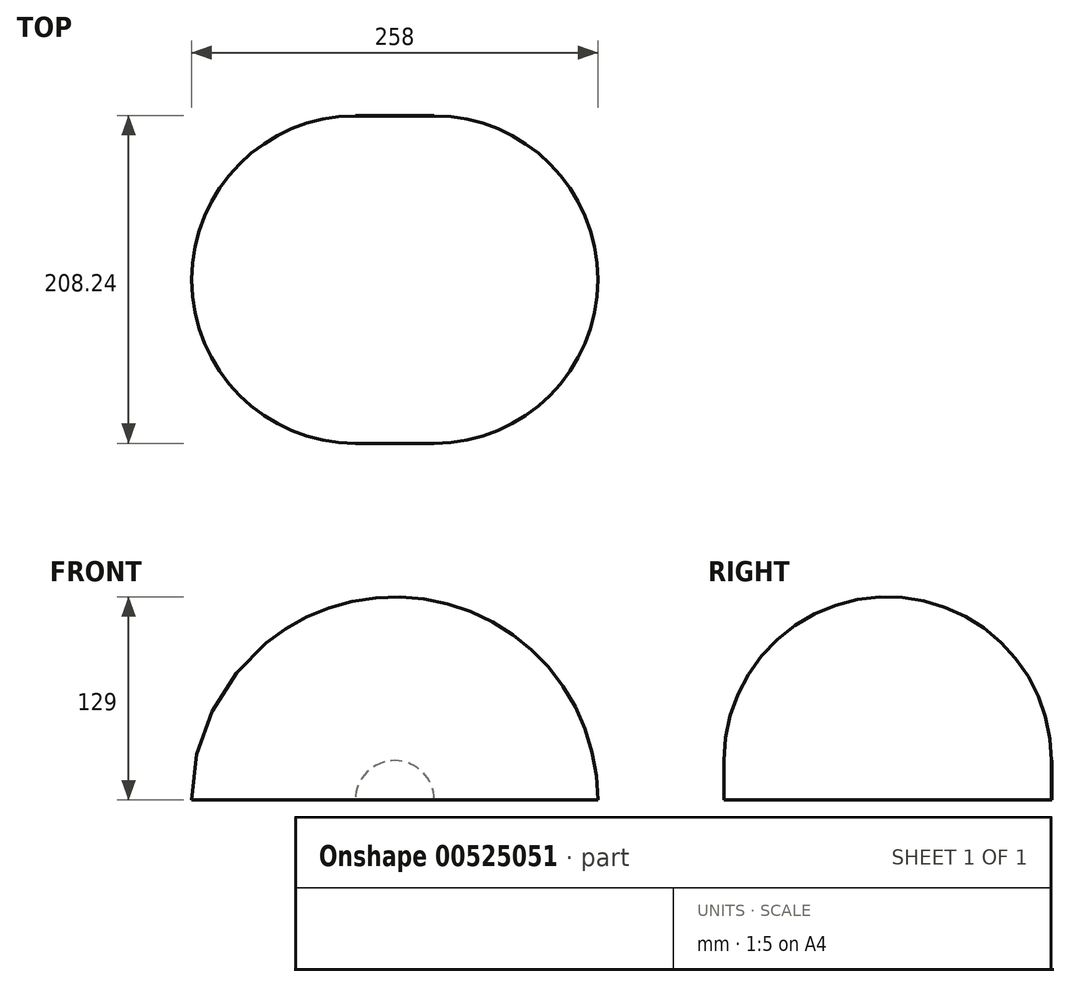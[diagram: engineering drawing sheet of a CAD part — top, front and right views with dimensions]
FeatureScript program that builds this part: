
annotation { "Feature Type Name" : "Feature", "Feature Type Description" : "" }
export const myFeature = defineFeature(function(context is Context, id is Id, definition is map)
    precondition{}
    {
        {
            var Q0;
            Q0=qCreatedBy(makeId("Right.planeOp"),FACE);
            var sketch = newSketch(context, id + "F0", { "sketchPlane" : qUnion([Q0])});
            skArc(sketch, "E0", {"start": v(104, 0) * mm, "mid": v(0, 104) * mm, "end": v(-104, 0) * mm});
            skLineSegment(sketch, "E1.bottom", {"start": v(104, 0) * mm, "end": v(104.24, 0) * mm});
            skLineSegment(sketch, "E1.top", {"start": v(-104, -25) * mm, "end": v(104.24, -25) * mm});
            skLineSegment(sketch, "E1.left", {"start": v(-104, 0) * mm, "end": v(-104, -25) * mm});
            skLineSegment(sketch, "E1.right", {"start": v(104.24, 0) * mm, "end": v(104.24, -25) * mm});
            skSolve(sketch);
        }
        {
            var Q0;
            Q0=makeQuery(id+"F0.imprint","IMPRINT",FACE,{"disambiguationData":[TD([[makeQuery(id+"F0.imprint","IMPRINT",EDGE,{"derivedFrom":sQuery(id+"F0.wireOp",EDGE,"E0")}),1.0]])]});
            var Q1;
            Q1=sQuery(id+"F0.wireOp",EDGE,"E1.top");
            revolve(context, id + "F1", {"entities" : qUnion([Q0]), "axis" : qUnion([Q1]), "revolveType" : RevolveType.SYMMETRIC, "angle" : 180 * degree});
        }
    });
